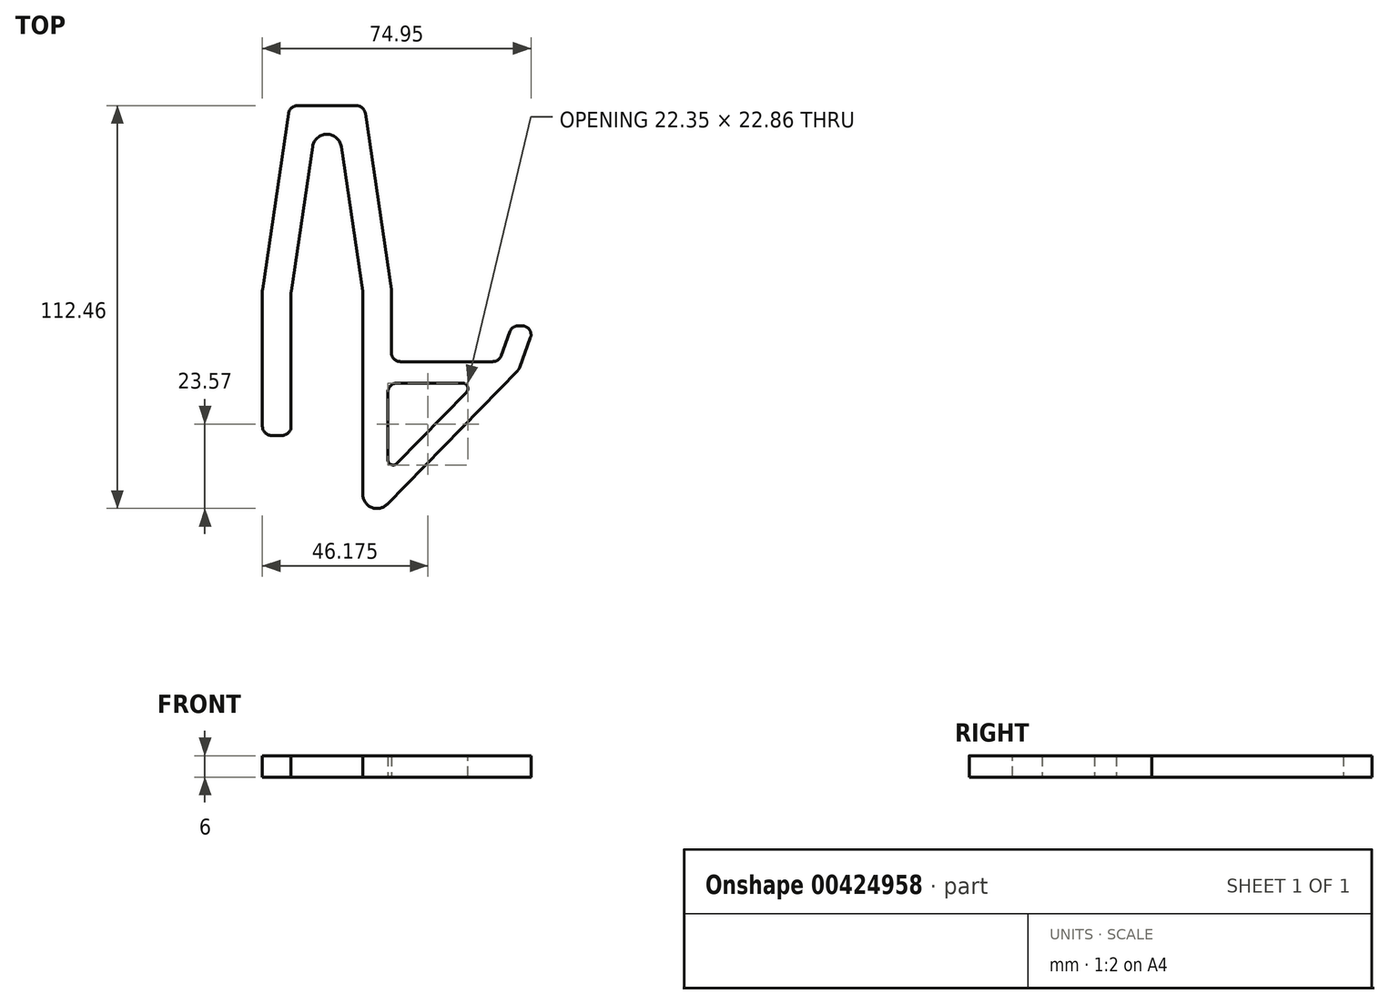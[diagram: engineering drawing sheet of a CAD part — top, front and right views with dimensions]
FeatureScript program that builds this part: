
annotation { "Feature Type Name" : "Feature", "Feature Type Description" : "" }
export const myFeature = defineFeature(function(context is Context, id is Id, definition is map)
    precondition{}
    {
        {
            var Q0;
            Q0=qCreatedBy(makeId("Top.planeOp"),FACE);
            var sketch = newSketch(context, id + "F0", { "sketchPlane" : qUnion([Q0])});
            skLineSegment(sketch, "E0", {"start": v(0, 0) * mm, "end": v(30, 0) * mm});
            skLineSegment(sketch, "E1", {"start": v(30, 0) * mm, "end": v(33.64, 10) * mm});
            skLineSegment(sketch, "E2", {"start": v(33.64, 10) * mm, "end": v(40.02, 10) * mm});
            skLineSegment(sketch, "E3", {"start": v(-8, -37) * mm, "end": v(-8, 19.41) * mm});
            skLineSegment(sketch, "E4", {"start": v(-8, 19.41) * mm, "end": v(-14, 60) * mm});
            skLineSegment(sketch, "E5", {"start": v(-22, 60) * mm, "end": v(-28, 19.41) * mm});
            skLineSegment(sketch, "E6", {"start": v(-28, 19.41) * mm, "end": v(-28, -20.59) * mm});
            skLineSegment(sketch, "E7", {"start": v(-28, -20.59) * mm, "end": v(-36, -20.59) * mm});
            skLineSegment(sketch, "E8", {"start": v(-36, -20.59) * mm, "end": v(-36, 20) * mm});
            skLineSegment(sketch, "E9", {"start": v(-36, 20) * mm, "end": v(-28.4, 71.46) * mm});
            skLineSegment(sketch, "E10", {"start": v(-28.4, 71.46) * mm, "end": v(-7.6, 71.46) * mm});
            skLineSegment(sketch, "E11", {"start": v(-7.6, 71.46) * mm, "end": v(0, 20) * mm});
            skLineSegment(sketch, "E12", {"start": v(0, 20) * mm, "end": v(0, 0) * mm});
            skArc(sketch, "E13", {"start": v(-14, 60) * mm, "mid": v(-18, 63.46) * mm, "end": v(-22, 60) * mm});
            skLineSegment(sketch, "E14", {"start": v(40.02, 10) * mm, "end": v(35.64, -2.05) * mm});
            skArc(sketch, "E15", {"start": v(-8, -37) * mm, "mid": v(-5.5, -40.7) * mm, "end": v(-1.14, -39.8) * mm});
            skLineSegment(sketch, "E16", {"start": v(35.64, -2.05) * mm, "end": v(-1.14, -39.8) * mm});
            skLineSegment(sketch, "E17", {"start": v(30, 0) * mm, "end": v(35.64, -2.05) * mm, "construction": true});
            skLineSegment(sketch, "E18", {"start": v(-1, -6) * mm, "end": v(-1, -31.06) * mm});
            skLineSegment(sketch, "E19", {"start": v(-1, -31.06) * mm, "end": v(23.41, -6) * mm});
            skLineSegment(sketch, "E20", {"start": v(23.41, -6) * mm, "end": v(-1, -6) * mm});
            skSolve(sketch);
        }
        {
            var Q0;
            Q0=makeQuery(id+"F0.imprint","IMPRINT",FACE,{"disambiguationData":[TD([[makeQuery(id+"F0.imprint","IMPRINT",EDGE,{"derivedFrom":sQuery(id+"F0.wireOp",EDGE,"E0")}),-1.0]])]});
            extrude(context, id + "F1", {"entities" : qUnion([Q0]), "depth" : 6 * mm});
        }
        {
            var Q0;
            Q0=makeQuery(id+"F1.opExtrude","SWEPT_EDGE",EDGE,{"disambiguationData":[OSD([sQuery(id+"F0.wireOp",EDGE,"E8"),sQuery(id+"F0.wireOp",EDGE,"E9")])]});
            var Q1;
            Q1=makeQuery(id+"F1.opExtrude","SWEPT_EDGE",EDGE,{"disambiguationData":[OSD([sQuery(id+"F0.wireOp",EDGE,"E9"),sQuery(id+"F0.wireOp",EDGE,"E10")])]});
            var Q2;
            Q2=makeQuery(id+"F1.opExtrude","SWEPT_EDGE",EDGE,{"disambiguationData":[OSD([sQuery(id+"F0.wireOp",EDGE,"E10"),sQuery(id+"F0.wireOp",EDGE,"E11")])]});
            var Q3;
            Q3=makeQuery(id+"F1.opExtrude","SWEPT_EDGE",EDGE,{"disambiguationData":[OSD([sQuery(id+"F0.wireOp",EDGE,"E1"),sQuery(id+"F0.wireOp",EDGE,"E2")])]});
            var Q4;
            Q4=makeQuery(id+"F1.opExtrude","SWEPT_EDGE",EDGE,{"disambiguationData":[OSD([sQuery(id+"F0.wireOp",EDGE,"E2"),sQuery(id+"F0.wireOp",EDGE,"E14")])]});
            var Q5;
            Q5=makeQuery(id+"F1.opExtrude","SWEPT_EDGE",EDGE,{"disambiguationData":[OSD([sQuery(id+"F0.wireOp",EDGE,"E3"),sQuery(id+"F0.wireOp",EDGE,"E4")])]});
            var Q6;
            Q6=makeQuery(id+"F1.opExtrude","SWEPT_EDGE",EDGE,{"disambiguationData":[OSD([sQuery(id+"F0.wireOp",EDGE,"E11"),sQuery(id+"F0.wireOp",EDGE,"E12")])]});
            var Q7;
            Q7=makeQuery(id+"F1.opExtrude","SWEPT_EDGE",EDGE,{"disambiguationData":[OSD([sQuery(id+"F0.wireOp",EDGE,"E0"),sQuery(id+"F0.wireOp",EDGE,"E12")])]});
            var Q8;
            Q8=makeQuery(id+"F1.opExtrude","SWEPT_EDGE",EDGE,{"disambiguationData":[OSD([sQuery(id+"F0.wireOp",EDGE,"E0"),sQuery(id+"F0.wireOp",EDGE,"E1")])]});
            var Q9;
            Q9=makeQuery(id+"F1.opExtrude","SWEPT_EDGE",EDGE,{"disambiguationData":[OSD([sQuery(id+"F0.wireOp",EDGE,"E14"),sQuery(id+"F0.wireOp",EDGE,"E16")])]});
            var Q10;
            Q10=makeQuery(id+"F1.opExtrude","SWEPT_EDGE",EDGE,{"disambiguationData":[OSD([sQuery(id+"F0.wireOp",EDGE,"E18"),sQuery(id+"F0.wireOp",EDGE,"E20")])]});
            var Q11;
            Q11=makeQuery(id+"F1.opExtrude","SWEPT_EDGE",EDGE,{"disambiguationData":[OSD([sQuery(id+"F0.wireOp",EDGE,"E7"),sQuery(id+"F0.wireOp",EDGE,"E8")])]});
            var Q12;
            Q12=makeQuery(id+"F1.opExtrude","SWEPT_EDGE",EDGE,{"disambiguationData":[OSD([sQuery(id+"F0.wireOp",EDGE,"E6"),sQuery(id+"F0.wireOp",EDGE,"E7")])]});
            var Q13;
            Q13=makeQuery(id+"F1.opExtrude","SWEPT_EDGE",EDGE,{"disambiguationData":[OSD([sQuery(id+"F0.wireOp",EDGE,"E5"),sQuery(id+"F0.wireOp",EDGE,"E6")])]});
            fillet(context, id + "F2", {"entities" : qUnion([Q0, Q1, Q2, Q3, Q4, Q5, Q6, Q7, Q8, Q9, Q10, Q11, Q12, Q13]), "radius" : 2.5 * mm, "tangentPropagation" : true, "allowEdgeOverflow" : false});
        }
        {
            var Q0;
            Q0=makeQuery(id+"F1.opExtrude","SWEPT_EDGE",EDGE,{"disambiguationData":[OSD([sQuery(id+"F0.wireOp",EDGE,"E19"),sQuery(id+"F0.wireOp",EDGE,"E20")])]});
            var Q1;
            Q1=makeQuery(id+"F1.opExtrude","SWEPT_EDGE",EDGE,{"disambiguationData":[OSD([sQuery(id+"F0.wireOp",EDGE,"E18"),sQuery(id+"F0.wireOp",EDGE,"E19")])]});
            fillet(context, id + "F3", {"entities" : qUnion([Q0, Q1]), "radius" : 1.5 * mm, "tangentPropagation" : true, "allowEdgeOverflow" : false});
        }
    });
